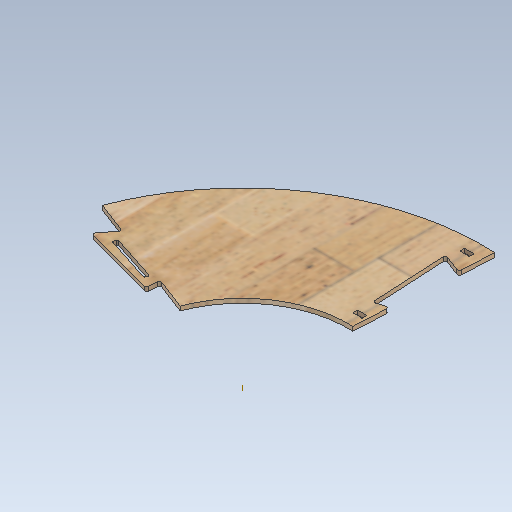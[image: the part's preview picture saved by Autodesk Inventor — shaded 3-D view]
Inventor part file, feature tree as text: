
AUTODESK INVENTOR PART (.ipt)
format: ipt  version: 2020 (Build 240168000, 168)  size: 466,432 bytes
history: native  units: mm
features: extrude x5, sketch x4, pattern_circular x3, plane x1, mirror x1
ambient origin geometry x8: Origin, YZ Plane, XZ Plane, XY Plane, X Axis, Y Axis, Z Axis, Center Point
bodies: Body1 (feature_tree)
feature tree (14):
  extrude  "Extrusion3"  Depth=6.5mm
  extrude  "Extrusion4"  Depth=2.666667mm
  extrude  "Extrusion5"  Depth=1.333333mm
  sketch  "Sketch5"  dims[d25=2.666667mm d32=1.333333mm]
  extrude  "Extrusion7"  TaperAngle=0.0deg  [1 undecoded]
  plane  "Work Plane1"
  pattern_circular  "Circular Pattern2"  [2 undecoded]
  pattern_circular  "Circular Pattern3"  Angle=90.0deg  [1 undecoded]
  mirror  "Mirror3"
  pattern_circular  "Circular Pattern4"  [2 undecoded]
  extrude  "Extrusion10"  TaperAngle=90.0deg  [1 undecoded]
  sketch  "Sketch2"  dims[d15=6.0mm d16=0.0mm d21=6.5mm]
  sketch  "Sketch3"  dims[d23=66.666667mm d24=2.666667mm]
  sketch  "Sketch6"  dims[d33=1.333333mm d38=0.0mm d39=0.0mm d40=3.25mm d41=90.0deg d42=3.25mm d43=90.0deg d47=50.0mm d49=360.0deg d52=4.363323mm d54=10.0mm d55=0.0mm d60=0.872665mm d61=12.566371mm d62=13.439035mm d63=2.666667mm d64=0.523599mm d66=0.523599mm d67=2.666667mm d68=2.666667mm d70=12.566371mm d71=12.566371mm d84=300.14mm d85=682.72mm d86=491.43mm d87=150.07mm d88=341.36mm d89=4.363323mm d90=1.919862mm d91=1.919862mm d94=300.14mm d95=682.72mm d104=6.5mm d105=12.0mm d108=1.333333mm d109=1.333333mm d110=1.333333mm d111=1.333333mm d112=0.0mm d113=0.0mm d114=0.0mm d141=3.25mm d145=20.0mm d146=12.566371mm d149=145.0mm d150=90.0deg d151=90.0deg d152=90.0deg d153=90.0deg d154=20.0mm d155=25.132741mm d157=20.0mm d158=25.132741mm d160=0.0mm d161=0.0mm]
note: 7 required parameter values undecoded (feature->parameter linkage not recoverable at this tier; creation-order binding heuristic only, values carry confidence <= 0.55)
